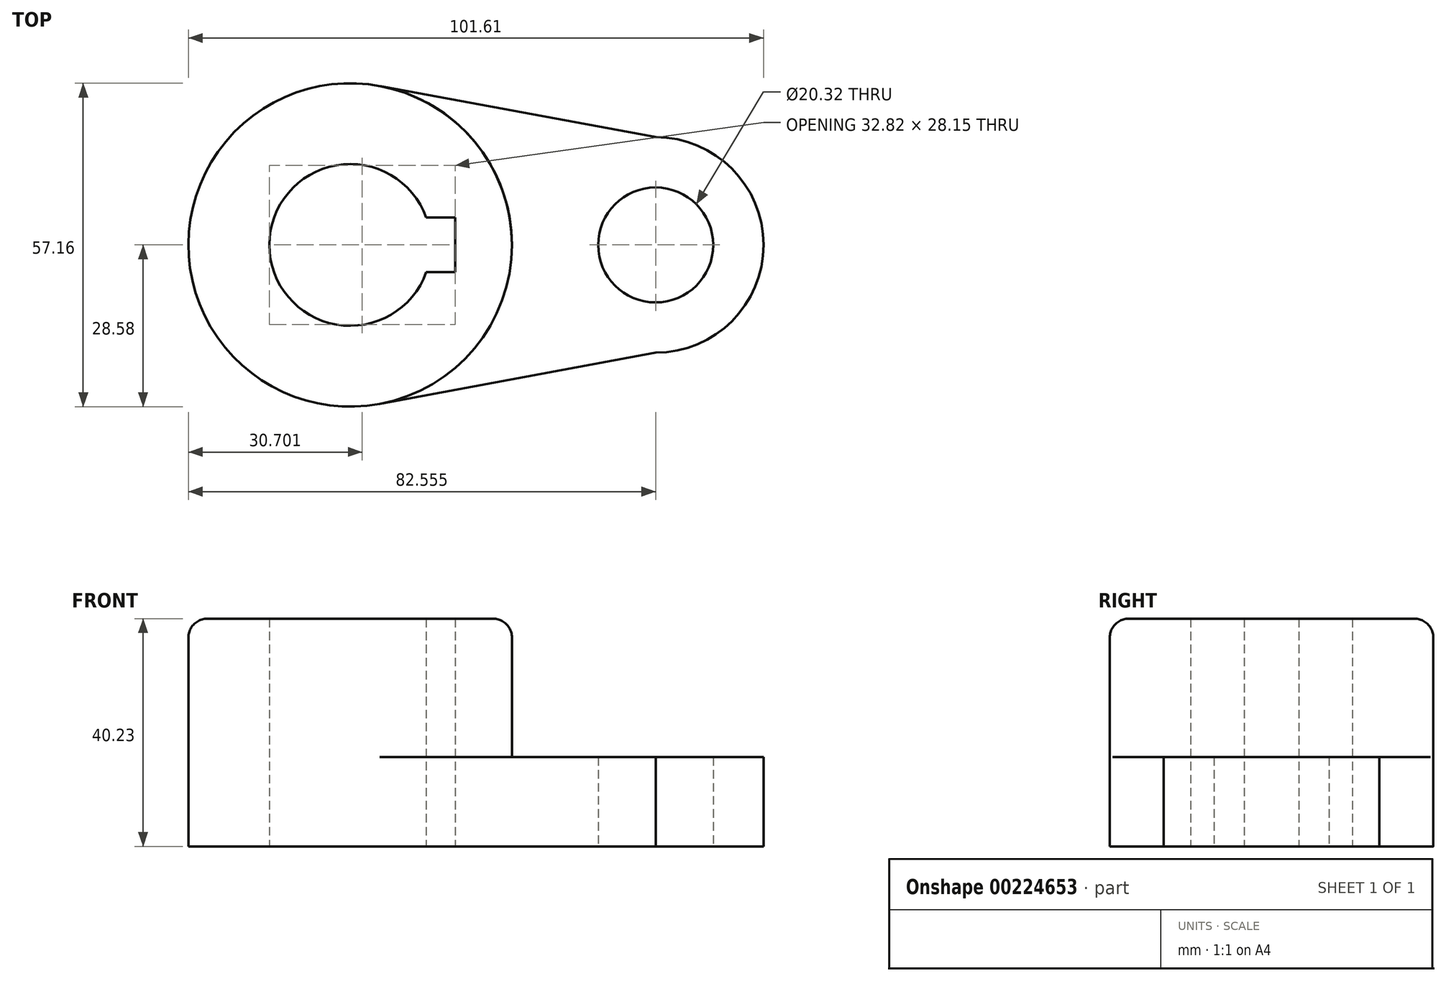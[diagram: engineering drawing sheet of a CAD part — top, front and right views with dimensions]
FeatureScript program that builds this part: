
annotation { "Feature Type Name" : "Feature", "Feature Type Description" : "" }
export const myFeature = defineFeature(function(context is Context, id is Id, definition is map)
    precondition{}
    {
        {
            var Q0;
            Q0=qCreatedBy(makeId("Top.planeOp"),FACE);
            var sketch = newSketch(context, id + "F0", { "sketchPlane" : qUnion([Q0])});
            skCircle(sketch, "E0", {"center": v(0, 0) * mm, "radius": 28.58 * mm});
            skCircle(sketch, "E1", {"center": v(0, 0) * mm, "radius": 14.29 * mm});
            skArc(sketch, "E2", {"start": v(53.97, 19.05) * mm, "mid": v(73.03, 0) * mm, "end": v(53.98, -19.05) * mm});
            skLineSegment(sketch, "E3", {"start": v(53.97, 19.05) * mm, "end": v(5.21, 28.1) * mm});
            skLineSegment(sketch, "E4", {"start": v(53.97, -19.05) * mm, "end": v(5.21, -28.1) * mm});
            skCircle(sketch, "E5", {"center": v(53.98, 0) * mm, "radius": 10.16 * mm});
            skLineSegment(sketch, "E6.bottom", {"start": v(18.53, 4.83) * mm, "end": v(-18.53, 4.83) * mm});
            skLineSegment(sketch, "E6.top", {"start": v(18.53, -4.83) * mm, "end": v(-18.53, -4.83) * mm});
            skLineSegment(sketch, "E6.left", {"start": v(18.53, 4.83) * mm, "end": v(18.53, -4.83) * mm});
            skLineSegment(sketch, "E6.right", {"start": v(-18.53, 4.83) * mm, "end": v(-18.53, -4.83) * mm});
            skSolve(sketch);
        }
        {
            var Q0;
            {var subQ10=sQuery(id+"F0.wireOp",EDGE,"E6.left");Q0=makeQuery(id+"F0.imprint","IMPRINT",FACE,{"disambiguationData":[TD([[makeQuery(id+"F0.imprint","IMPRINT",EDGE,{"derivedFrom":subQ10}),1.0]])]});}
            var Q1;
            {var subQ5=sQuery(id+"F0.wireOp",EDGE,"E6.right");Q1=makeQuery(id+"F0.imprint","IMPRINT",FACE,{"disambiguationData":[TD([[makeQuery(id+"F0.imprint","IMPRINT",EDGE,{"derivedFrom":subQ5}),1.0]])]});}
            extrude(context, id + "F1", {"entities" : qUnion([Q0, Q1]), "depth" : 40.23 * mm});
        }
        {
            var Q0;
            Q0 = qSketchRegion(id + "F0", true);
            extrude(context, id + "F2", {"entities" : qUnion([Q0]), "operationType" : NewBodyOperationType.ADD, "depth" : 15.77 * mm});
        }
        {
            var Q0;
            Q0=makeQuery(id+"F1.opExtrude","CAP_EDGE",EDGE,{"disambiguationData":[OSD([sQuery(id+"F0.wireOp",EDGE,"E0")])],"isStart":false});
            fillet(context, id + "F3", {"entities" : qUnion([Q0]), "radius" : 3.3 * mm, "tangentPropagation" : true, "allowEdgeOverflow" : false});
        }
    });
